# Revit family: Lixil-Grohe-Listra-Tub_Spout_with_Diverter-106206_0
name_source: partatom
category: Plumbing Fixtures
units: mm (PartAtom-declared; Revit-internal decimal feet)

## family parameters
Cut with Voids When Loaded = No
Enable Cutting in Views = Yes
Host = Face
Maintain Annotation Orientation = No
OmniClass Number = 23.45.55.17
OmniClass Title = Mixing Faucets
Part Type = Normal
Room Calculation Point = No
Round Connector Dimension = Use Diameter
Shared = No

## types (1)
- Listra Tub Spout with Diverter
    Assembly Code = D2010400
    Brand = Grohe
    CW Connection = Yes
    Collection = Listra
    Default Elevation = 0"
    Depth = 7 3/8"
    Description = Tub Spout with Diverter
    Finish = Metal - Grohe - Chrome
    HW Connection = Yes
    Keynote = 22 40 00
    Manufacturer = LIXIL
    Model = 106206_0
    Product Documentation Link = https://www.grohe.us
    Product Name = Listra Tub Spout with Diverter
    Product Page URL = https://www.grohe.us
    URL = https://www.grohe.us
    Vent Connection = No
    Version = 2023 - v1.0a
    Warranty URL = https://www.grohe.us
    Waste Connection = No
    Width = 2 3/4"

## geometry (parser evidence)
native form markers: Sweep x1
no freeform markers — native parametric forms only
